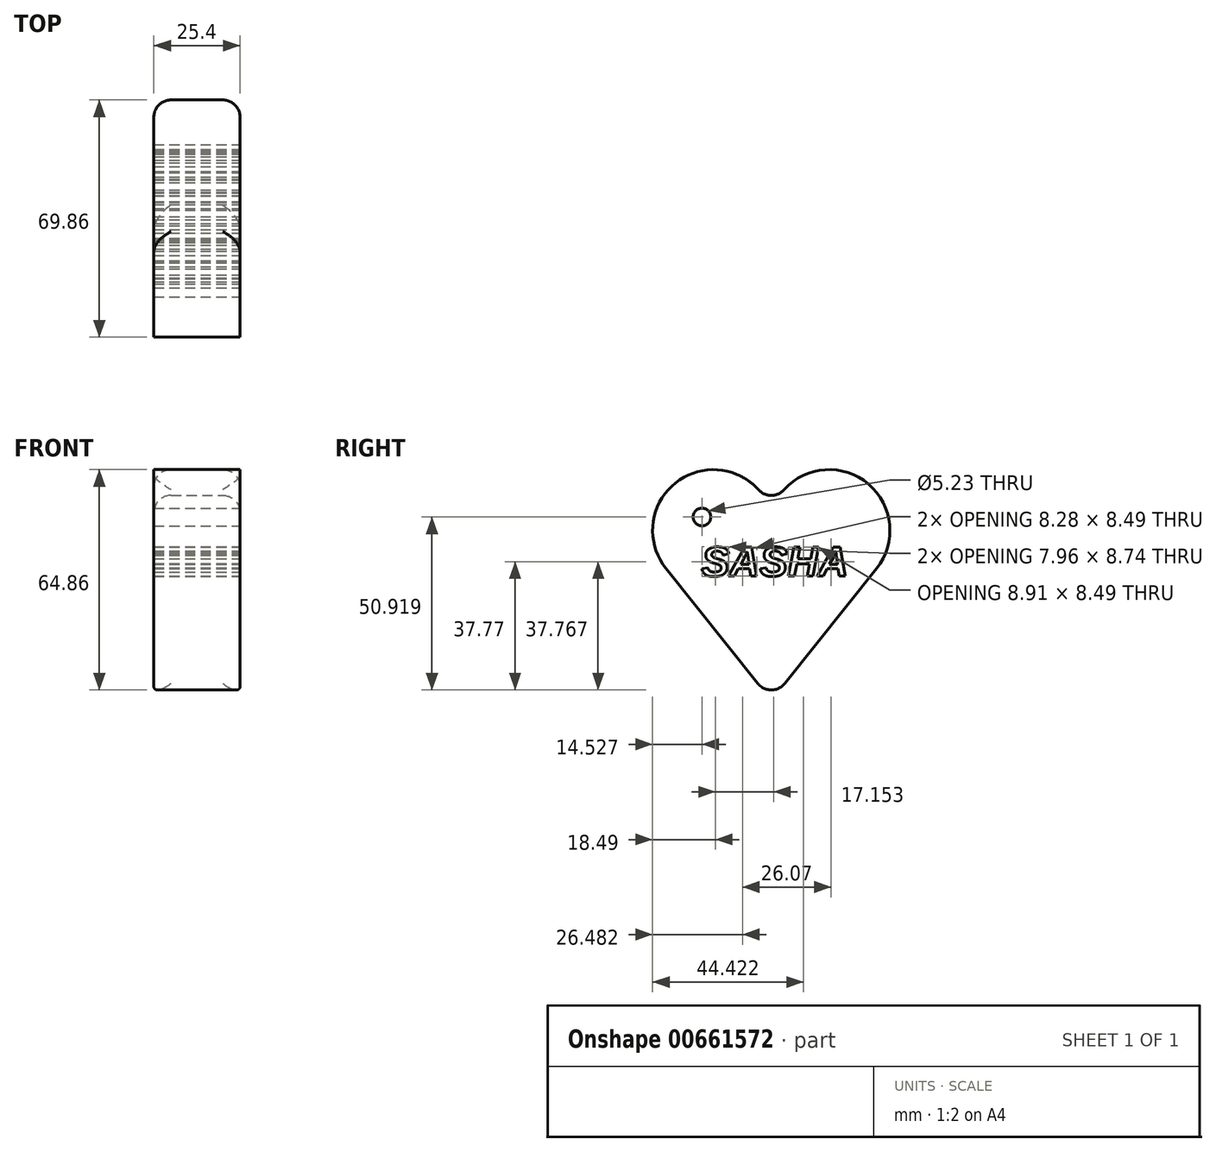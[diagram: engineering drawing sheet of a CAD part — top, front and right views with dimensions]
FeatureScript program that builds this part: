
annotation { "Feature Type Name" : "Feature", "Feature Type Description" : "" }
export const myFeature = defineFeature(function(context is Context, id is Id, definition is map)
    precondition{}
    {
        {
            var Q0;
            Q0=qCreatedBy(makeId("Right.planeOp"),FACE);
            var sketch = newSketch(context, id + "F0", { "sketchPlane" : qUnion([Q0])});
            skLineSegment(sketch, "E0", {"start": v(0, -38.87) * mm, "end": v(31.03, 0) * mm});
            skArc(sketch, "E1", {"start": v(31.03, 0) * mm, "mid": v(25.48, 26.94) * mm, "end": v(0, 16.6) * mm});
            skArc(sketch, "E2.MirrorCS", {"start": v(-31.03, 0) * mm, "mid": v(-25.48, 26.94) * mm, "end": v(0, 16.6) * mm});
            skLineSegment(sketch, "E3.MirrorCS", {"start": v(0, -38.87) * mm, "end": v(-31.03, 0) * mm});
            skSolve(sketch);
        }
        {
            var Q0;
            Q0=qSketchRegion(id+"F0",true);
            extrude(context, id + "F1", {"entities" : qUnion([Q0]), "depth" : 25.4 * mm, "offsetDistance" : 25.4 * mm});
        }
        {
            var Q0;
            Q0=makeQuery(id+"F1.opExtrude","CAP_FACE",FACE,{"disambiguationData":[OSD([sQuery(id+"F0.wireOp",EDGE,"E0"),sQuery(id+"F0.wireOp",EDGE,"E1"),sQuery(id+"F0.wireOp",EDGE,"E2.MirrorCS"),sQuery(id+"F0.wireOp",EDGE,"E3.MirrorCS")])],"isStart":false});
            var sketch = newSketch(context, id + "F2", { "sketchPlane" : qUnion([Q0])});
            skText(sketch, "E4", { "text": "SASHA\n", "fontName": "Arimo-BoldItalic.ttf"});
            const initialGuessF2  = {"E4": [-0.02057, -0.00229, 1, 0, 0.00889]};
            skSetInitialGuess(sketch, initialGuessF2);
            skSolve(sketch);
        }
        {
            var Q0;
            Q0=qSketchRegion(id+"F2",true);
            extrude(context, id + "F3", {"entities" : qUnion([Q0]), "operationType" : NewBodyOperationType.REMOVE, "oppositeDirection" : true, "depth" : 152.4 * mm, "offsetDistance" : 25.4 * mm});
        }
        {
            var Q0;
            Q0=makeQuery(id+"F1.opExtrude","SWEPT_FACE",FACE,{"disambiguationData":[OSD([sQuery(id+"F0.wireOp",EDGE,"E1")])]});
            var Q1;
            Q1=makeQuery(id+"F1.opExtrude","SWEPT_EDGE",EDGE,{"disambiguationData":[OSD([sQuery(id+"F0.wireOp",EDGE,"E0"),sQuery(id+"F0.wireOp",EDGE,"E3.MirrorCS")])]});
            fillet(context, id + "F4", {"entities" : qUnion([Q0, Q1]), "radius" : 5.08 * mm, "tangentPropagation" : true, "allowEdgeOverflow" : false});
        }
        {
            var Q0;
            {var subQ0=sQuery(id+"F0.wireOp",EDGE,"E2.MirrorCS");var subQ1=sQuery(id+"F0.wireOp",EDGE,"E0");var subQ2=sQuery(id+"F0.wireOp",EDGE,"E3.MirrorCS");var subQ3=sQuery(id+"F0.wireOp",EDGE,"E1");Q0=makeQuery(id+"F3.boolean.opBoolean","SPLIT",FACE,{"disambiguationData":[TD([makeQuery(id+"F1.opExtrude","SWEPT_FACE",FACE,{"disambiguationData":[OSD([subQ1])]})])],"derivedFrom":makeQuery(id+"F1.opExtrude","CAP_FACE",FACE,{"disambiguationData":[OSD([subQ1,subQ3,subQ0,subQ2])],"isStart":false})});}
            var sketch = newSketch(context, id + "F5", { "sketchPlane" : qUnion([Q0])});
            skCircle(sketch, "E5", {"center": v(-20.4, 15.1) * mm, "radius": 2.62 * mm});
            skSolve(sketch);
        }
        {
            var Q0;
            Q0=makeQuery(id+"F5.imprint","IMPRINT",FACE,{"disambiguationData":[TD([[makeQuery(id+"F5.imprint","IMPRINT",EDGE,{"derivedFrom":sQuery(id+"F5.wireOp",EDGE,"E5")}),1.0]])]});
            extrude(context, id + "F6", {"entities" : qUnion([Q0]), "operationType" : NewBodyOperationType.REMOVE, "oppositeDirection" : true, "depth" : 152.4 * mm, "offsetDistance" : 25.4 * mm});
        }
    });
